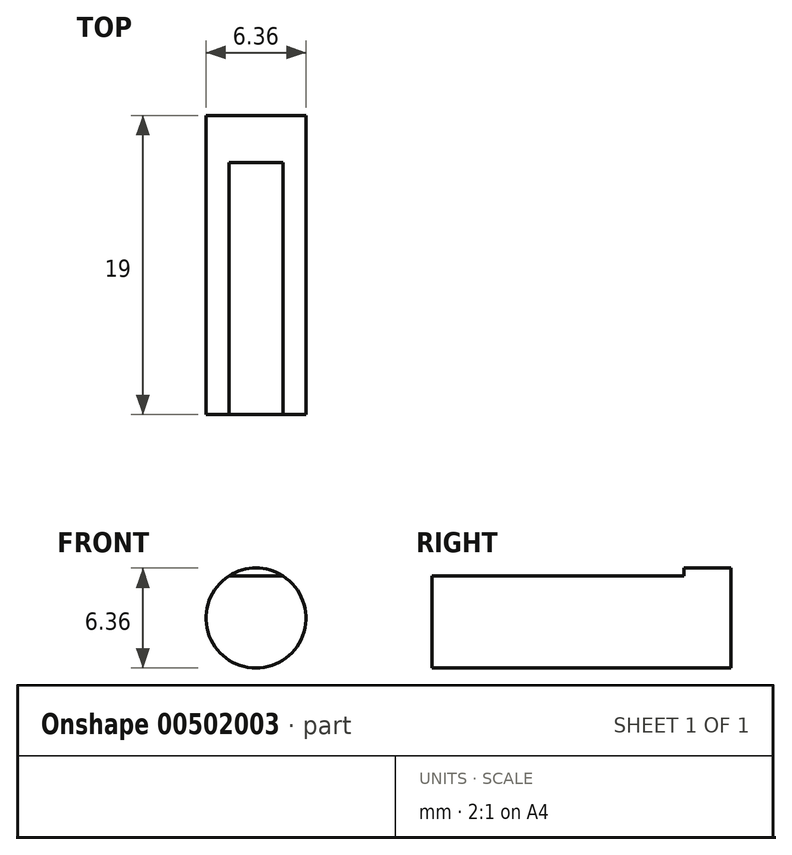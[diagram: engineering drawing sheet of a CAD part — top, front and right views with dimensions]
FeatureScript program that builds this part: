
annotation { "Feature Type Name" : "Feature", "Feature Type Description" : "" }
export const myFeature = defineFeature(function(context is Context, id is Id, definition is map)
    precondition{}
    {
        {
            var Q0;
            Q0=qCreatedBy(makeId("Front.planeOp"),FACE);
            var sketch = newSketch(context, id + "F0", { "sketchPlane" : qUnion([Q0])});
            skCircle(sketch, "E0", {"center": v(0, 0) * mm, "radius": 3.17 * mm});
            skSolve(sketch);
        }
        {
            var Q0;
            Q0 = qSketchRegion(id + "F0", true);
            extrude(context, id + "F1", {"entities" : qUnion([Q0]), "depth" : 19 * mm});
        }
        {
            var Q0;
            Q0=qCreatedBy(makeId("Right.planeOp"),FACE);
            var sketch = newSketch(context, id + "F2", { "sketchPlane" : qUnion([Q0])});
            skLineSegment(sketch, "E1", {"start": v(0, 0) * mm, "end": v(-51.17, 0) * mm, "construction": true});
            skLineSegment(sketch, "E2", {"start": v(-23, 2.67) * mm, "end": v(-3, 2.67) * mm});
            skLineSegment(sketch, "E3", {"start": v(-3, 2.68) * mm, "end": v(-3, 7.68) * mm});
            skLineSegment(sketch, "E4", {"start": v(-3, 7.68) * mm, "end": v(-23, 2.68) * mm});
            skSolve(sketch);
        }
        {
            var Q0;
            Q0=makeQuery(id+"F2.imprint","IMPRINT",FACE,{"disambiguationData":[TD([[makeQuery(id+"F2.imprint","IMPRINT",EDGE,{"derivedFrom":sQuery(id+"F2.wireOp",EDGE,"E2")}),1.0]])]});
            extrude(context, id + "F3", {"entities" : qUnion([Q0]), "operationType" : NewBodyOperationType.REMOVE, "endBound" : BoundingType.SYMMETRIC, "oppositeDirection" : true, "depth" : 25 * mm});
        }
    });
